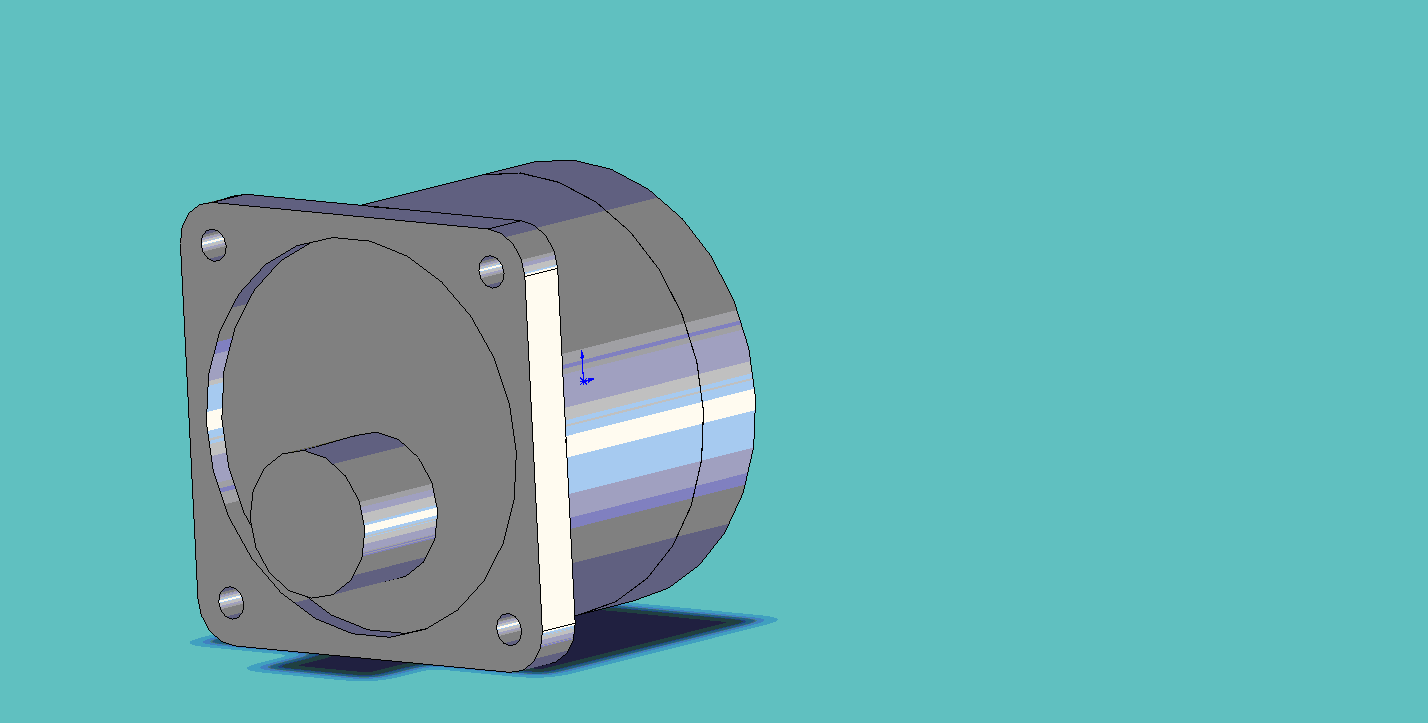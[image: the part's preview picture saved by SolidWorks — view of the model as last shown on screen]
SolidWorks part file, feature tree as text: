
SOLIDWORKS PART (.sldprt)
format: sldprt  version: not decoded by parser v0  size: 304,640 bytes
history: native  units: mm
features: sketch x5, plane x3, cut_extrude x2, material x1, revolve x1, extrude x1, fillet x1, cut_revolve x1 (+12 scaffold rows collapsed)
feature tree (27):
  scaffold x12  (default folders/planes/origin — collapsed)
  material  "Matériau <non spécifié>"
  plane  "Plan de face"
  plane  "Plan de dessus"
  plane  "Plan de droite"
  sketch  "Esquisse1"  dims[D1=30.0mm D2=29.98mm D3=5.4mm D4=19.6mm]
  revolve  "Révolution1"  Angle=360deg
  sketch  "Esquisse2"  dims[c1.D6=2.2mm c1.D2=30.0mm c1.D3=15.0mm c1.D4=15.0mm c1.D1=24.2mm c1.D5=30.0mm c2.D1=3.0mm]
  extrude  "Extrusion1"  Depth=3.4mm
  sketch  "Esquisse3"  dims[D1=27.0mm]
  cut_extrude  "Enlèv. mat.-Extru.1"  Depth=1.6mm
  fillet  "Congé1"  Radius=3mm
  sketch  "Esquisse4"  dims[D2=10.0mm D1=4.9mm]
  cut_extrude  "Extrusion2"  Depth=7.55mm
  sketch  "Esquisse5"  dims[D1=3.0mm D2=1.1mm D3=8.5mm D4=2.0mm D5=4.2mm D6=8.0mm]
  cut_revolve  "Enlèvement de matière-Révolution1"  Angle=360deg
decode coverage: 11 of 11 modeling features carry decoded parameters
note: suppression state not decoded; provenance and decode notes live in map.json
